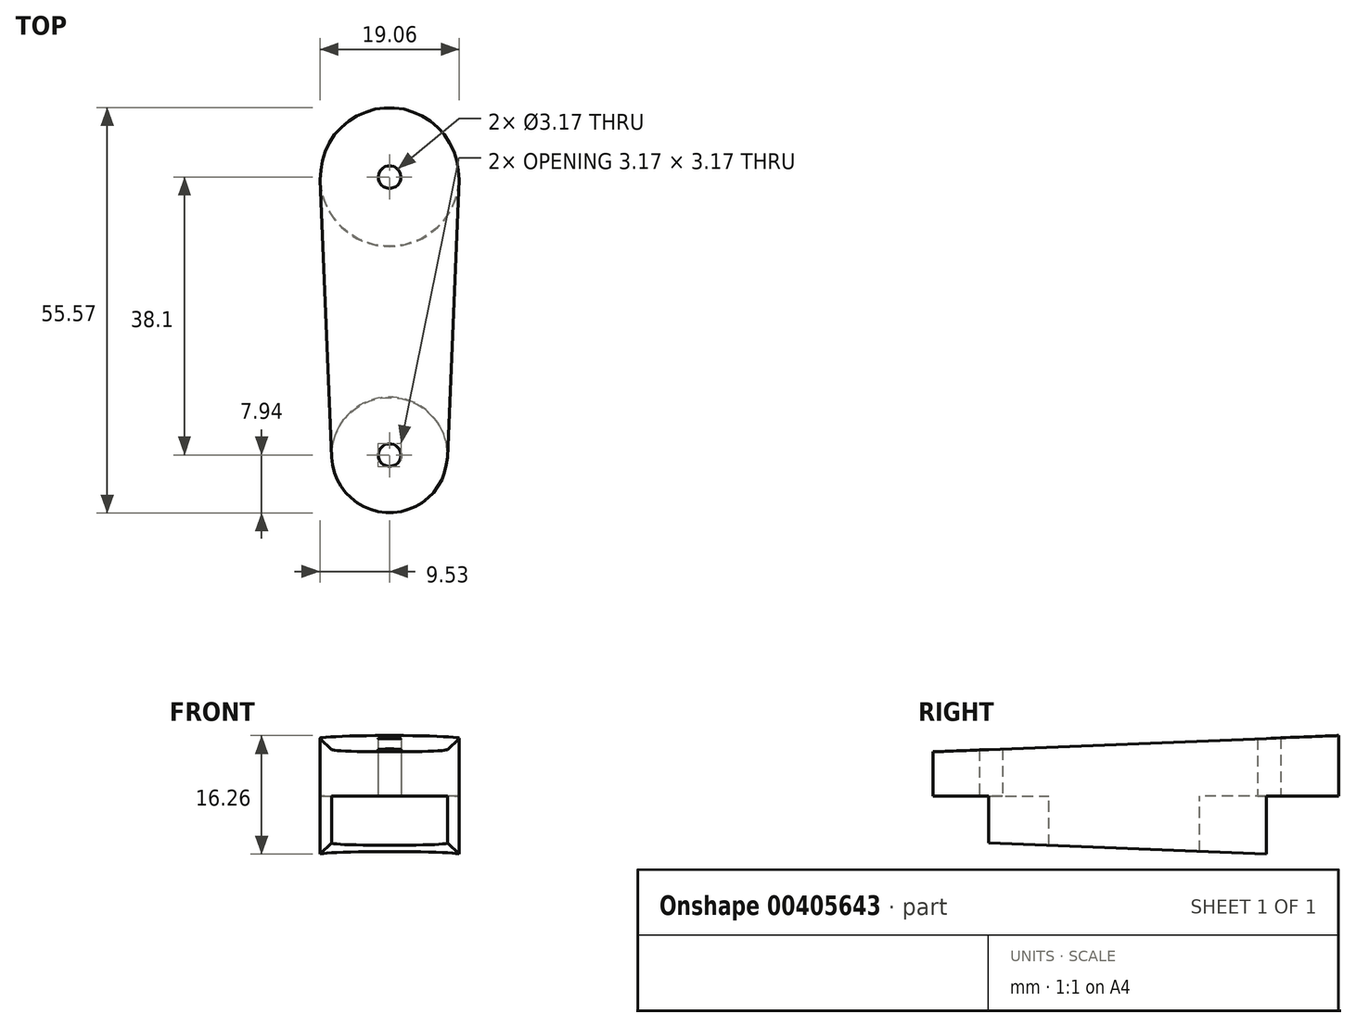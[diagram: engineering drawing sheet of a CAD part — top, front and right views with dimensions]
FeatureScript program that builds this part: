
annotation { "Feature Type Name" : "Feature", "Feature Type Description" : "" }
export const myFeature = defineFeature(function(context is Context, id is Id, definition is map)
    precondition{}
    {
        {
            var Q0;
            Q0=qCreatedBy(makeId("Top.planeOp"),FACE);
            var sketch = newSketch(context, id + "F0", { "sketchPlane" : qUnion([Q0])});
            skArc(sketch, "E0", {"start": v(9.52, -0.4) * mm, "mid": v(0, 9.52) * mm, "end": v(-9.52, -0.4) * mm});
            skLineSegment(sketch, "E1", {"start": v(0, 0) * mm, "end": v(0, -44.45) * mm, "construction": true});
            skCircle(sketch, "E2", {"center": v(0, 0) * mm, "radius": 1.59 * mm});
            skCircle(sketch, "E3", {"center": v(0, -38.1) * mm, "radius": 1.59 * mm});
            skLineSegment(sketch, "E4", {"start": v(-9.52, -0.4) * mm, "end": v(-7.93, -38.43) * mm});
            skLineSegment(sketch, "E5", {"start": v(9.52, -0.4) * mm, "end": v(7.93, -38.43) * mm});
            skArc(sketch, "E6", {"start": v(-7.93, -38.43) * mm, "mid": v(0, -46.04) * mm, "end": v(7.93, -38.43) * mm});
            skSolve(sketch);
        }
        {
            var Q0;
            Q0=qCreatedBy(makeId("Right.planeOp"),FACE);
            var sketch = newSketch(context, id + "F1", { "sketchPlane" : qUnion([Q0])});
            skLineSegment(sketch, "E7", {"start": v(0, 35.76) * mm, "end": v(0, -37.23) * mm, "construction": true});
            skLineSegment(sketch, "E8", {"start": v(-64.8, 0) * mm, "end": v(46.31, 0) * mm, "construction": true});
            skCircle(sketch, "E9", {"center": v(0, 0) * mm, "radius": 7.94 * mm, "construction": true});
            skLineSegment(sketch, "E10.0", {"start": v(0, 7.94) * mm, "end": v(0, 3.18) * mm});
            skLineSegment(sketch, "E11.trimOffspring", {"start": v(-0.16, 7.94) * mm, "end": v(9.52, 8.33) * mm});
            skLineSegment(sketch, "E12.trimOffspring", {"start": v(0, -7.94) * mm, "end": v(9.53, -8.33) * mm});
            skLineSegment(sketch, "E13.0", {"start": v(9.52, 8.33) * mm, "end": v(9.53, -8.33) * mm});
            skLineSegment(sketch, "E14.trimOffspring", {"start": v(0, -7.94) * mm, "end": v(0, -7.94) * mm});
            skLineSegment(sketch, "E15", {"start": v(-46.04, 6.1) * mm, "end": v(-46.04, -6.1) * mm});
            skPoint(sketch, "E16.orphan", {"position": v(-38.1, 37.23) * mm});
            skPoint(sketch, "E17.orphan", {"position": v(-38.1, -37.23) * mm});
            skLineSegment(sketch, "E18.0", {"start": v(-39.69, 6.35) * mm, "end": v(-39.69, 6.35) * mm});
            skLineSegment(sketch, "E19.trimOffspring", {"start": v(-39.69, 6.35) * mm, "end": v(0, 7.94) * mm});
            skLineSegment(sketch, "E20.trimOffspring", {"start": v(-39.69, -6.35) * mm, "end": v(0, -7.94) * mm});
            skLineSegment(sketch, "E21.trimOffspring", {"start": v(-39.69, -6.35) * mm, "end": v(-39.69, -6.35) * mm});
            skLineSegment(sketch, "E22.trimOffspring", {"start": v(-39.69, 6.35) * mm, "end": v(-46.04, 6.1) * mm});
            skLineSegment(sketch, "E23.trimOffspring", {"start": v(-39.69, -6.35) * mm, "end": v(-46.04, -6.1) * mm});
            skPoint(sketch, "E24.center.orphan", {"position": v(-38.1, 0) * mm});
            skSolve(sketch);
        }
        {
            var Q0;
            Q0=qSketchRegion(id+"F0",true);
            extrude(context, id + "F2", {"entities" : qUnion([Q0]), "endBound" : BoundingType.SYMMETRIC, "depth" : 25.4 * mm});
        }
        {
            var Q0;
            Q0=qSketchRegion(id+"F1",true);
            extrude(context, id + "F3", {"entities" : qUnion([Q0]), "operationType" : NewBodyOperationType.INTERSECT, "endBound" : BoundingType.SYMMETRIC, "depth" : 25.4 * mm});
        }
        {
            var Q0;
            Q0=qCreatedBy(makeId("Top.planeOp"),FACE);
            cPlane(context, id + "F4", {"entities" : qUnion([Q0]), "cplaneType" : CPlaneType.OFFSET, "offset" : 0 * mm, "width" : 152.4 * mm, "height" : 152.4 * mm});
        }
        {
            var Q0;
            Q0=qCreatedBy(id+"F4.planeOp",FACE);
            var sketch = newSketch(context, id + "F5", { "sketchPlane" : qUnion([Q0])});
            skArc(sketch, "E25.0", {"start": v(9.52, -0.4) * mm, "mid": v(0, 9.52) * mm, "end": v(-9.52, -0.4) * mm});
            skCircle(sketch, "E26", {"center": v(0, 0) * mm, "radius": 9.53 * mm});
            skCircle(sketch, "E27.0", {"center": v(0, -38.1) * mm, "radius": 1.59 * mm});
            skCircle(sketch, "E28", {"center": v(0, -38.1) * mm, "radius": 7.94 * mm});
            skSolve(sketch);
        }
        {
            var Q0;
            Q0 = qSketchRegion(id + "F5", true);
            extrude(context, id + "F6", {"entities" : qUnion([Q0]), "operationType" : NewBodyOperationType.REMOVE, "oppositeDirection" : true, "depth" : 25.4 * mm});
        }
    });
